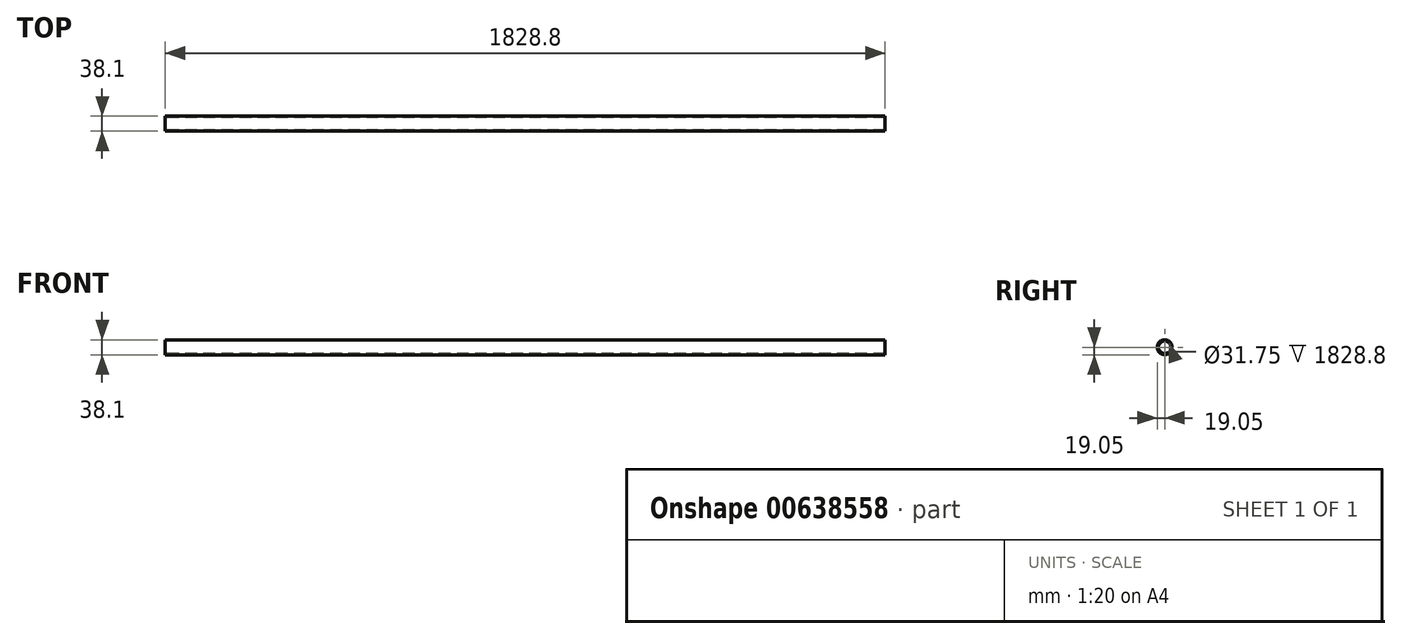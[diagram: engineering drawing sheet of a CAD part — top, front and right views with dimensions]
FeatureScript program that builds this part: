
annotation { "Feature Type Name" : "Feature", "Feature Type Description" : "" }
export const myFeature = defineFeature(function(context is Context, id is Id, definition is map)
    precondition{}
    {
        {
            var Q0;
            Q0=qCreatedBy(makeId("Right.planeOp"),FACE);
            var sketch = newSketch(context, id + "F0", { "sketchPlane" : qUnion([Q0])});
            skCircle(sketch, "E0", {"center": v(0, 0) * mm, "radius": 19.05 * mm});
            skCircle(sketch, "E1", {"center": v(0, 0) * mm, "radius": 15.88 * mm});
            skSolve(sketch);
        }
        {
            var Q0;
            Q0=makeQuery(id+"F0.imprint","IMPRINT",FACE,{"disambiguationData":[TD([[makeQuery(id+"F0.imprint","IMPRINT",EDGE,{"derivedFrom":sQuery(id+"F0.wireOp",EDGE,"E0")}),1.0]])]});
            var Q1;
            Q1=sQuery(id+"F0.wireOp",EDGE,"E1");
            var Q2;
            Q2=sQuery(id+"F0.wireOp",EDGE,"E0");
            extrude(context, id + "F1", {"entities" : qUnion([Q0]), "surfaceEntities" : qUnion([Q1, Q2]), "endBound" : BoundingType.SYMMETRIC, "depth" : 1828.8 * mm, "offsetDistance" : 25.4 * mm});
        }
    });
